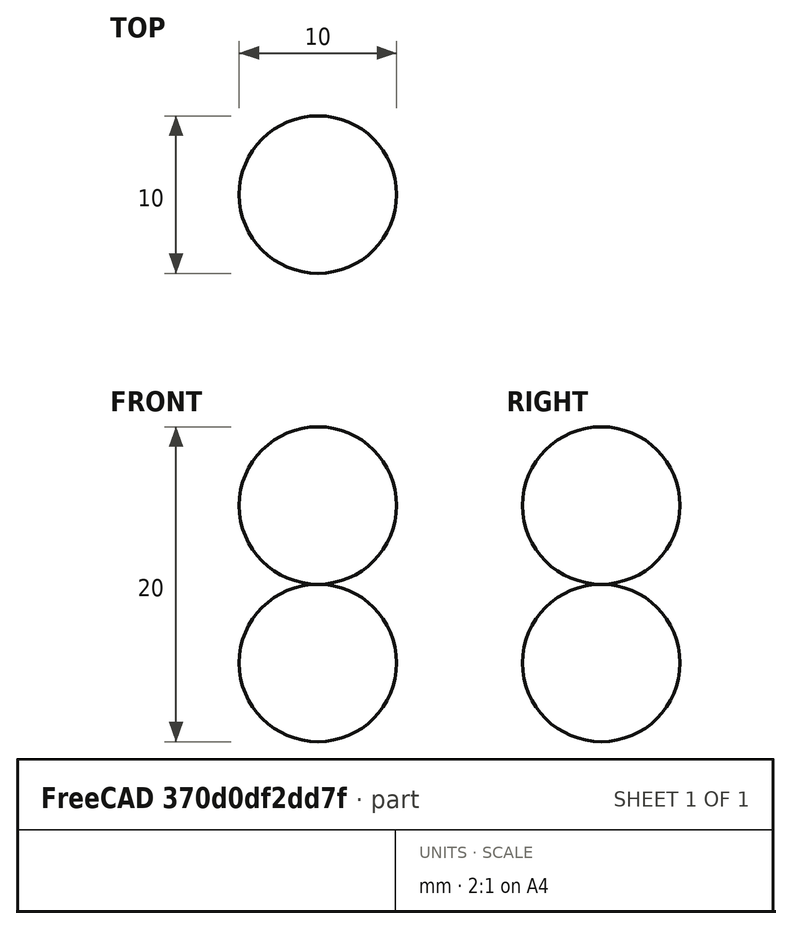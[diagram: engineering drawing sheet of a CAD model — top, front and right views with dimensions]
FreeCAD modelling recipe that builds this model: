
FCSTD DOCUMENT  (FreeCAD 1.1R20260325 (Git shallow))
Label: brokenexplodecompound
Comment: Repro for FreeCAD issue #29733 (Part::transformShape regression in 1.2-dev). Relicensed CC0 by author for inclusion in FreeCAD integration test suite.
License: CC0-1.0
LicenseURL: https://creativecommons.org/publicdomain/zero/1.0/
objects: Part::Sphere×2, Part::FeaturePython×2, Part::Compound×1, App::DocumentObjectGroup×1
note: 5 computed .brp shape members not serialized (recipe doc carries the construction recipe); baked Part::Feature solids carry a one-line shape summary decoded from their .brp

FEATURE [Part::Sphere] Sphere
  Angle1 = -90
  Angle2 = 90
  Angle3 = 360
  AttacherType = Attacher::AttachEngine3D
  Radius = 5
FEATURE [Part::Sphere] Sphere001
  Angle1 = -90
  Angle2 = 90
  Angle3 = 360
  AttacherType = Attacher::AttachEngine3D
  Placement = pos=(0,0,10) rot=(0,0,1;0rad)
  Radius = 5
FEATURE [Part::Compound] Compound
  Links = -> [Sphere,Sphere001]
FEATURE [Part::FeaturePython] Compound_child0  label="Compound.0"  # WARN: FeaturePython — macro-defined, semantics opaque (R4)
  Base = -> Compound
  FilterType = 1
  Invert = false
  OverrideMaxVal = 0
  WindowFrom = 80
  WindowTo = 100
  items = 0
FEATURE [Part::FeaturePython] Compound_child1  label="Compound.1"  # WARN: FeaturePython — macro-defined, semantics opaque (R4)
  Base = -> Compound
  FilterType = 1
  Invert = false
  OverrideMaxVal = 0
  WindowFrom = 80
  WindowTo = 100
  items = 1
FEATURE [App::DocumentObjectGroup] GrExplode_Compound  label="Exploded Compound"
  Group = -> [Compound_child0,Compound_child1]
